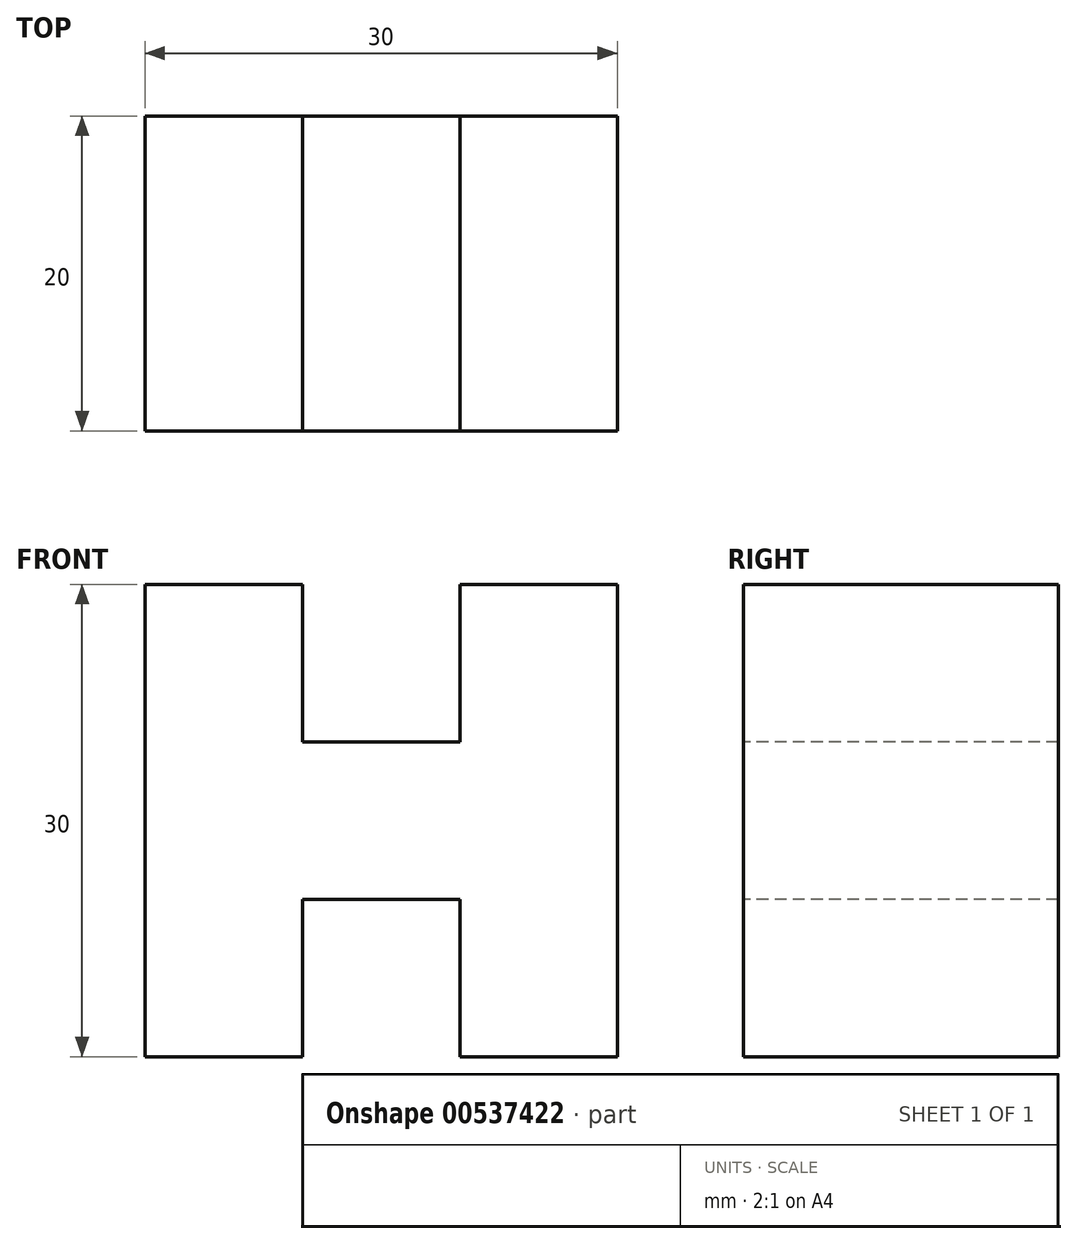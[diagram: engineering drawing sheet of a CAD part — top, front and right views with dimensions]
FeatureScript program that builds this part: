
annotation { "Feature Type Name" : "Feature", "Feature Type Description" : "" }
export const myFeature = defineFeature(function(context is Context, id is Id, definition is map)
    precondition{}
    {
        {
            var Q0;
            Q0=qCreatedBy(makeId("Top.planeOp"),FACE);
            var sketch = newSketch(context, id + "F0", { "sketchPlane" : qUnion([Q0])});
            skLineSegment(sketch, "E0.bottom", {"start": v(-61.95, -42.1) * mm, "end": v(-31.95, -42.1) * mm});
            skLineSegment(sketch, "E0.top", {"start": v(-61.95, -22.1) * mm, "end": v(-31.95, -22.1) * mm});
            skLineSegment(sketch, "E0.left", {"start": v(-61.95, -42.1) * mm, "end": v(-61.95, -22.1) * mm});
            skLineSegment(sketch, "E0.right", {"start": v(-31.95, -42.1) * mm, "end": v(-31.95, -22.1) * mm});
            skSolve(sketch);
        }
        {
            var Q0;
            Q0=makeQuery(id+"F0.imprint","IMPRINT",FACE,{"disambiguationData":[TD([[makeQuery(id+"F0.imprint","IMPRINT",EDGE,{"derivedFrom":sQuery(id+"F0.wireOp",EDGE,"E0.bottom")}),1.0]])]});
            extrude(context, id + "F1", {"entities" : qUnion([Q0]), "depth" : 30 * mm, "offsetDistance" : 25 * mm});
        }
        {
            var Q0;
            Q0=makeQuery(id+"F1.opExtrude","SWEPT_FACE",FACE,{"disambiguationData":[OSD([sQuery(id+"F0.wireOp",EDGE,"E0.bottom")])]});
            var sketch = newSketch(context, id + "F2", { "sketchPlane" : qUnion([Q0])});
            skLineSegment(sketch, "E1", {"start": v(-61.95, 0) * mm, "end": v(-51.95, 0) * mm});
            skLineSegment(sketch, "E2", {"start": v(-51.95, 0) * mm, "end": v(-51.95, 10) * mm});
            skLineSegment(sketch, "E3", {"start": v(-51.95, 10) * mm, "end": v(-41.95, 10) * mm});
            skLineSegment(sketch, "E4", {"start": v(-41.95, 10) * mm, "end": v(-41.95, 0) * mm});
            skLineSegment(sketch, "E5", {"start": v(-41.95, 0) * mm, "end": v(-31.95, 0) * mm});
            skLineSegment(sketch, "E6", {"start": v(-61.95, 30) * mm, "end": v(-51.95, 30) * mm});
            skLineSegment(sketch, "E7", {"start": v(-51.95, 30) * mm, "end": v(-51.95, 20) * mm});
            skLineSegment(sketch, "E8", {"start": v(-51.95, 20) * mm, "end": v(-41.95, 20) * mm});
            skLineSegment(sketch, "E9", {"start": v(-41.95, 20) * mm, "end": v(-41.95, 30) * mm});
            skLineSegment(sketch, "E10", {"start": v(-41.95, 30) * mm, "end": v(-31.95, 30) * mm});
            skSolve(sketch);
        }
        {
            var Q0;
            {var subQ0=sQuery(id+"F2.wireOp",EDGE,"E7");Q0=makeQuery(id+"F2.imprint","IMPRINT",FACE,{"disambiguationData":[TD([[makeQuery(id+"F2.imprint","IMPRINT",EDGE,{"derivedFrom":subQ0}),1.0]])]});}
            var Q1;
            {var subQ0=sQuery(id+"F2.wireOp",EDGE,"E2");Q1=makeQuery(id+"F2.imprint","IMPRINT",FACE,{"disambiguationData":[TD([[makeQuery(id+"F2.imprint","IMPRINT",EDGE,{"derivedFrom":subQ0}),-1.0]])]});}
            extrude(context, id + "F3", {"entities" : qUnion([Q0, Q1]), "operationType" : NewBodyOperationType.REMOVE, "endBound" : BoundingType.THROUGH_ALL, "oppositeDirection" : true, "depth" : 25 * mm, "offsetDistance" : 25 * mm});
        }
    });
